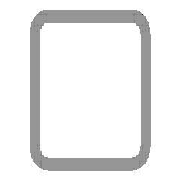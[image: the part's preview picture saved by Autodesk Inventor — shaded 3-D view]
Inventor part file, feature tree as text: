
AUTODESK INVENTOR PART (.ipt)
format: ipt  version: 2021 (Build 250183000, 183)  size: 130,560 bytes
history: native  units: mm (DEFAULTED — no unit token found)
features: other x4, sketch x3, extrude x1, plane x1
ambient origin geometry x8: Origin, YZ Plane, XZ Plane, XY Plane, X Axis, Y Axis, Z Axis, Center Point
bodies: Solid1 (feature_tree)
feature tree (9):
  parser-record x1  (decoder bookkeeping rows leaked as tree rows — omitted from the tree; the rows remain in map.json)
  other  "Driven Length"
  other  "Plano inicial"
  other  "Plano final"
  extrude  "Corpo"  TaperAngle=0.0deg  [1 undecoded]
  sketch  "Esboço"  dims[d11=50.8mm d12=4.7625mm d13=-0.0mm d14=2236.067977mm d15=25.4mm d16=25.4mm d17=9.525mm d18=90.0deg d19=2236.067977mm]
  sketch  "Sketch3"  dims[d3=2236.067977mm d4=0.0mm]
  plane  "Work Plane3"
  sketch  "Sketch4"  dims[d10=50.8mm]
note: 1 required parameter value undecoded (feature->parameter linkage not recoverable at this tier; creation-order binding heuristic only, values carry confidence <= 0.55)
